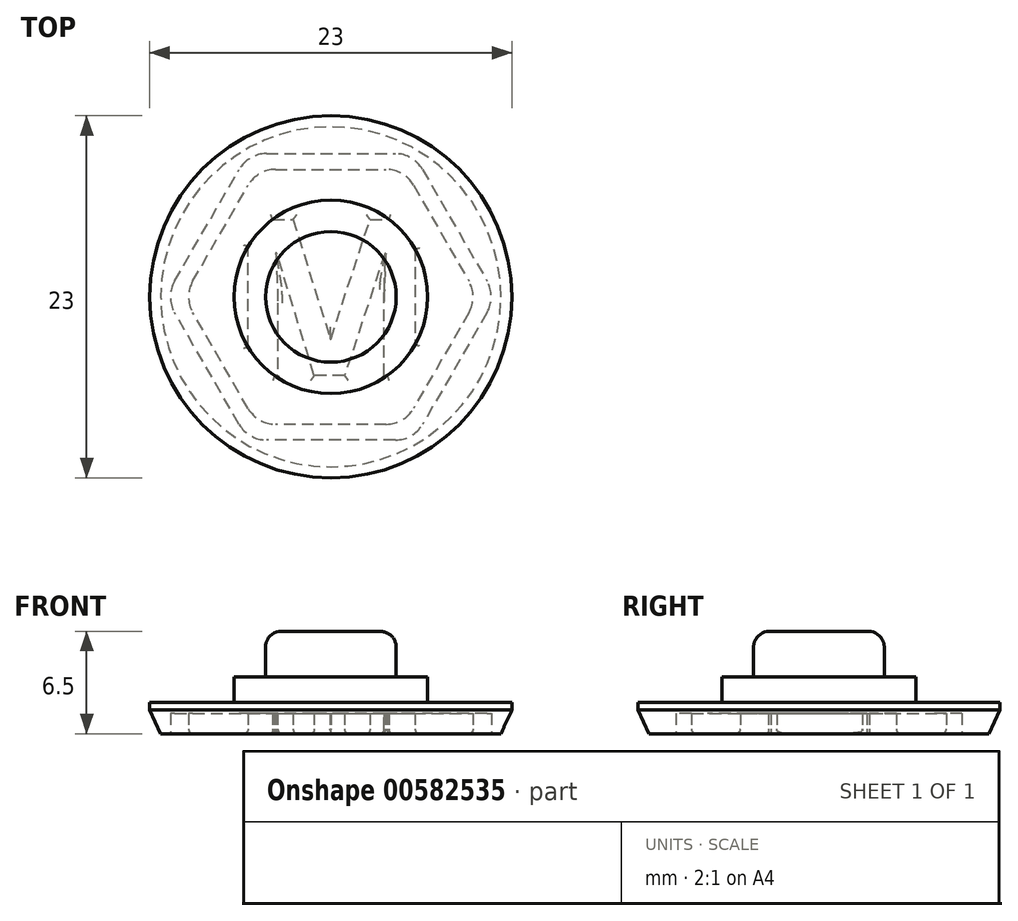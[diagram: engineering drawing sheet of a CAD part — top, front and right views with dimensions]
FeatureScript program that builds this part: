
annotation { "Feature Type Name" : "Feature", "Feature Type Description" : "" }
export const myFeature = defineFeature(function(context is Context, id is Id, definition is map)
    precondition{}
    {
        {
            var Q0;
            Q0=qCreatedBy(makeId("Top.planeOp"),FACE);
            var sketch = newSketch(context, id + "F0", { "sketchPlane" : qUnion([Q0])});
            skCircle(sketch, "E0", {"center": v(0, 0) * mm, "radius": 11.5 * mm});
            skCircle(sketch, "E1", {"center": v(0, 0) * mm, "radius": 4.15 * mm});
            skCircle(sketch, "E2.0", {"center": v(0, 0) * mm, "radius": 6.15 * mm});
            skSolve(sketch);
        }
        {
            var Q0;
            Q0=makeQuery(id+"F0.imprint","IMPRINT",FACE,{"disambiguationData":[TD([[makeQuery(id+"F0.imprint","IMPRINT",EDGE,{"derivedFrom":sQuery(id+"F0.wireOp",EDGE,"E0")}),1.0]])]});
            extrude(context, id + "F1", {"entities" : qUnion([Q0]), "depth" : 2 * mm, "offsetDistance" : 25 * mm});
        }
        {
            var Q0;
            Q0=makeQuery(id+"F0.imprint","IMPRINT",FACE,{"disambiguationData":[TD([[makeQuery(id+"F0.imprint","IMPRINT",EDGE,{"derivedFrom":sQuery(id+"F0.wireOp",EDGE,"E1")}),-1.0]])]});
            extrude(context, id + "F2", {"entities" : qUnion([Q0]), "operationType" : NewBodyOperationType.ADD, "depth" : 3.6 * mm, "offsetDistance" : 25 * mm});
        }
        {
            var Q0;
            Q0=makeQuery(id+"F0.imprint","IMPRINT",FACE,{"disambiguationData":[TD([[makeQuery(id+"F0.imprint","IMPRINT",EDGE,{"derivedFrom":sQuery(id+"F0.wireOp",EDGE,"E1")}),1.0]])]});
            extrude(context, id + "F3", {"entities" : qUnion([Q0]), "operationType" : NewBodyOperationType.ADD, "depth" : 6.5 * mm, "offsetDistance" : 25 * mm});
        }
        {
            var Q0;
            Q0=makeQuery(id+"F0.imprint","IMPRINT",FACE,{"disambiguationData":[TD([[makeQuery(id+"F0.imprint","IMPRINT",EDGE,{"derivedFrom":sQuery(id+"F0.wireOp",EDGE,"E0")}),1.0]])]});
            var sketch = newSketch(context, id + "F4", { "sketchPlane" : qUnion([Q0])});
            skCircle(sketch, "E3.cCircle", {"center": v(0, 0) * mm, "radius": 9.1 * mm, "construction": true});
            skLineSegment(sketch, "E3.0", {"start": v(9.92, -1) * mm, "end": v(5.83, -8.1) * mm});
            skLineSegment(sketch, "E3.1", {"start": v(4.1, -9.1) * mm, "end": v(-4.1, -9.1) * mm});
            skLineSegment(sketch, "E3.2", {"start": v(-5.83, -8.1) * mm, "end": v(-9.92, -1) * mm});
            skLineSegment(sketch, "E3.3", {"start": v(-9.92, 1) * mm, "end": v(-5.83, 8.1) * mm});
            skLineSegment(sketch, "E3.4", {"start": v(-4.1, 9.1) * mm, "end": v(4.1, 9.1) * mm});
            skLineSegment(sketch, "E3.5", {"start": v(5.83, 8.1) * mm, "end": v(9.92, 1) * mm});
            skPoint(sketch, "E3.0.midPoint", {"position": v(7.87, -4.55) * mm});
            skLineSegment(sketch, "E4.0", {"start": v(5.25, 7.1) * mm, "end": v(8.77, 1) * mm});
            skLineSegment(sketch, "E4.1", {"start": v(3.52, -8.1) * mm, "end": v(-3.52, -8.1) * mm});
            skLineSegment(sketch, "E4.2", {"start": v(-5.25, -7.1) * mm, "end": v(-8.77, -1) * mm});
            skLineSegment(sketch, "E4.3", {"start": v(8.77, -1) * mm, "end": v(5.25, -7.1) * mm});
            skLineSegment(sketch, "E4.4", {"start": v(-8.77, 1) * mm, "end": v(-5.25, 7.1) * mm});
            skLineSegment(sketch, "E4.5", {"start": v(-3.52, 8.1) * mm, "end": v(3.52, 8.1) * mm});
            skPoint(sketch, "E5.visualSharp", {"position": v(10.5, 0) * mm});
            skArc(sketch, "E5.filletArc", {"start": v(9.92, -1) * mm, "mid": v(10.2, 0) * mm, "end": v(9.92, 1) * mm});
            skPoint(sketch, "E6.visualSharp", {"position": v(5.25, 9.1) * mm});
            skArc(sketch, "E6.filletArc", {"start": v(5.83, 8.1) * mm, "mid": v(5.1, 8.83) * mm, "end": v(4.1, 9.1) * mm});
            skPoint(sketch, "E7.visualSharp", {"position": v(-5.25, 9.1) * mm});
            skArc(sketch, "E7.filletArc", {"start": v(-4.1, 9.1) * mm, "mid": v(-5.1, 8.83) * mm, "end": v(-5.83, 8.1) * mm});
            skPoint(sketch, "E8.visualSharp", {"position": v(-10.5, 0) * mm});
            skArc(sketch, "E8.filletArc", {"start": v(-9.92, 1) * mm, "mid": v(-10.2, 0) * mm, "end": v(-9.92, -1) * mm});
            skPoint(sketch, "E9.visualSharp", {"position": v(-5.25, -9.1) * mm});
            skArc(sketch, "E9.filletArc", {"start": v(-5.83, -8.1) * mm, "mid": v(-5.1, -8.83) * mm, "end": v(-4.1, -9.1) * mm});
            skPoint(sketch, "E10.visualSharp", {"position": v(5.25, -9.1) * mm});
            skArc(sketch, "E10.filletArc", {"start": v(4.1, -9.1) * mm, "mid": v(5.1, -8.83) * mm, "end": v(5.83, -8.1) * mm});
            skPoint(sketch, "E11.visualSharp", {"position": v(4.67, -8.1) * mm});
            skArc(sketch, "E11.filletArc", {"start": v(3.52, -8.1) * mm, "mid": v(4.52, -7.83) * mm, "end": v(5.25, -7.1) * mm});
            skPoint(sketch, "E12.visualSharp", {"position": v(4.67, 8.1) * mm});
            skArc(sketch, "E12.filletArc", {"start": v(5.25, 7.1) * mm, "mid": v(4.52, 7.83) * mm, "end": v(3.52, 8.1) * mm});
            skPoint(sketch, "E13.visualSharp", {"position": v(-4.67, 8.1) * mm});
            skArc(sketch, "E13.filletArc", {"start": v(-3.52, 8.1) * mm, "mid": v(-4.52, 7.83) * mm, "end": v(-5.25, 7.1) * mm});
            skPoint(sketch, "E14.visualSharp", {"position": v(-9.35, 0) * mm});
            skArc(sketch, "E14.filletArc", {"start": v(-8.77, 1) * mm, "mid": v(-9.04, 0) * mm, "end": v(-8.77, -1) * mm});
            skPoint(sketch, "E15.visualSharp", {"position": v(-4.67, -8.1) * mm});
            skArc(sketch, "E15.filletArc", {"start": v(-5.25, -7.1) * mm, "mid": v(-4.52, -7.83) * mm, "end": v(-3.52, -8.1) * mm});
            skPoint(sketch, "E16.visualSharp", {"position": v(9.35, 0) * mm});
            skArc(sketch, "E16.filletArc", {"start": v(8.77, -1) * mm, "mid": v(9.04, 0) * mm, "end": v(8.77, 1) * mm});
            skText(sketch, "E17", { "text": "M", "fontName": "OpenSans-Bold.ttf"});
            const initialGuessF4  = {"E17": [-0.0065, -0.005, 1, 0, 0.01]};
            skSetInitialGuess(sketch, initialGuessF4);
            skSolve(sketch);
        }
        {
            var Q0;
            Q0=makeQuery(id+"F4.imprint","IMPRINT",FACE,{"disambiguationData":[TD([[makeQuery(id+"F4.imprint","IMPRINT",EDGE,{"derivedFrom":sQuery(id+"F4.wireOp",EDGE,"E17.sketch_text.stroke-0")}),-1.0]])]});
            var Q1;
            Q1=makeQuery(id+"F4.imprint","IMPRINT",FACE,{"disambiguationData":[TD([[makeQuery(id+"F4.imprint","IMPRINT",EDGE,{"derivedFrom":sQuery(id+"F4.wireOp",EDGE,"E3.0")}),-1.0]])]});
            extrude(context, id + "F5", {"entities" : qUnion([Q0, Q1]), "operationType" : NewBodyOperationType.REMOVE, "depth" : 1.3 * mm, "offsetDistance" : 25 * mm});
        }
        {
            var Q0;
            Q0=makeQuery(id+"F1.opExtrude","CAP_EDGE",EDGE,{"disambiguationData":[OSD([sQuery(id+"F0.wireOp",EDGE,"E0")])],"isStart":true});
            chamfer(context, id + "F6", {"entities" : qUnion([Q0]), "chamferType" : ChamferType.TWO_OFFSETS, "width1" : 1.5 * mm, "oppositeDirection" : false, "width2" : 0.7 * mm, "tangentPropagation" : true});
        }
        {
            var Q0;
            Q0=makeQuery(id+"F3.opExtrude","CAP_EDGE",EDGE,{"disambiguationData":[OSD([sQuery(id+"F0.wireOp",EDGE,"E1")])],"isStart":false});
            fillet(context, id + "F7", {"entities" : qUnion([Q0]), "radius" : 1 * mm, "tangentPropagation" : true, "allowEdgeOverflow" : false});
        }
        {
            var Q0;
            Q0=makeQuery(id+"F5.boolean.opBoolean","COPY",EDGE,{"derivedFrom":makeQuery(id+"F5.opExtrude","CAP_EDGE",EDGE,{"disambiguationData":[OSD([sQuery(id+"F4.wireOp",EDGE,"E3.5")])],"isStart":true})});
            var Q1;
            Q1=makeQuery(id+"F5.boolean.opBoolean","COPY",EDGE,{"derivedFrom":makeQuery(id+"F5.opExtrude","CAP_EDGE",EDGE,{"disambiguationData":[OSD([sQuery(id+"F4.wireOp",EDGE,"E4.3")])],"isStart":true})});
            var Q2;
            Q2=makeQuery(id+"F5.boolean.opBoolean","COPY",EDGE,{"derivedFrom":makeQuery(id+"F5.opExtrude","CAP_EDGE",EDGE,{"disambiguationData":[OSD([sQuery(id+"F4.wireOp",EDGE,"4fd293f3-2c2e-4eb3-8031-e35e885f4dbc.sketch_text.stroke-5")])],"isStart":true})});
            var Q3;
            Q3=makeQuery(id+"F5.boolean.opBoolean","COPY",EDGE,{"derivedFrom":makeQuery(id+"F5.opExtrude","CAP_EDGE",EDGE,{"disambiguationData":[OSD([sQuery(id+"F4.wireOp",EDGE,"4fd293f3-2c2e-4eb3-8031-e35e885f4dbc.sketch_text.stroke-11")])],"isStart":true})});
            var Q4;
            Q4=makeQuery(id+"F5.boolean.opBoolean","COPY",EDGE,{"derivedFrom":makeQuery(id+"F5.opExtrude","CAP_EDGE",EDGE,{"disambiguationData":[OSD([sQuery(id+"F4.wireOp",EDGE,"4fd293f3-2c2e-4eb3-8031-e35e885f4dbc.sketch_text.stroke-10")])],"isStart":true})});
            var Q5;
            Q5=makeQuery(id+"F5.boolean.opBoolean","COPY",EDGE,{"derivedFrom":makeQuery(id+"F5.opExtrude","CAP_EDGE",EDGE,{"disambiguationData":[OSD([sQuery(id+"F4.wireOp",EDGE,"4fd293f3-2c2e-4eb3-8031-e35e885f4dbc.sketch_text.stroke-9")])],"isStart":true})});
            var Q6;
            Q6=makeQuery(id+"F5.boolean.opBoolean","COPY",EDGE,{"derivedFrom":makeQuery(id+"F5.opExtrude","CAP_EDGE",EDGE,{"disambiguationData":[OSD([sQuery(id+"F4.wireOp",EDGE,"4fd293f3-2c2e-4eb3-8031-e35e885f4dbc.sketch_text.stroke-7")])],"isStart":true})});
            var Q7;
            Q7=makeQuery(id+"F5.boolean.opBoolean","COPY",EDGE,{"derivedFrom":makeQuery(id+"F5.opExtrude","CAP_EDGE",EDGE,{"disambiguationData":[OSD([sQuery(id+"F4.wireOp",EDGE,"4fd293f3-2c2e-4eb3-8031-e35e885f4dbc.sketch_text.stroke-6")])],"isStart":true})});
            var Q8;
            Q8=makeQuery(id+"F5.boolean.opBoolean","COPY",EDGE,{"derivedFrom":makeQuery(id+"F5.opExtrude","CAP_EDGE",EDGE,{"disambiguationData":[OSD([sQuery(id+"F4.wireOp",EDGE,"4fd293f3-2c2e-4eb3-8031-e35e885f4dbc.sketch_text.stroke-3")])],"isStart":true})});
            var Q9;
            Q9=makeQuery(id+"F5.boolean.opBoolean","COPY",EDGE,{"derivedFrom":makeQuery(id+"F5.opExtrude","CAP_EDGE",EDGE,{"disambiguationData":[OSD([sQuery(id+"F4.wireOp",EDGE,"4fd293f3-2c2e-4eb3-8031-e35e885f4dbc.sketch_text.stroke-0")])],"isStart":true})});
            var Q10;
            Q10=makeQuery(id+"F5.boolean.opBoolean","COPY",EDGE,{"derivedFrom":makeQuery(id+"F5.opExtrude","CAP_EDGE",EDGE,{"disambiguationData":[OSD([sQuery(id+"F4.wireOp",EDGE,"4fd293f3-2c2e-4eb3-8031-e35e885f4dbc.sketch_text.stroke-17")])],"isStart":true})});
            var Q11;
            Q11=makeQuery(id+"F5.boolean.opBoolean","COPY",EDGE,{"derivedFrom":makeQuery(id+"F5.opExtrude","CAP_EDGE",EDGE,{"disambiguationData":[OSD([sQuery(id+"F4.wireOp",EDGE,"4fd293f3-2c2e-4eb3-8031-e35e885f4dbc.sketch_text.stroke-16")])],"isStart":true})});
            var Q12;
            Q12=makeQuery(id+"F5.boolean.opBoolean","COPY",EDGE,{"derivedFrom":makeQuery(id+"F5.opExtrude","CAP_EDGE",EDGE,{"disambiguationData":[OSD([sQuery(id+"F4.wireOp",EDGE,"4fd293f3-2c2e-4eb3-8031-e35e885f4dbc.sketch_text.stroke-13")])],"isStart":true})});
            var Q13;
            Q13=makeQuery(id+"F5.boolean.opBoolean","COPY",EDGE,{"derivedFrom":makeQuery(id+"F5.opExtrude","CAP_EDGE",EDGE,{"disambiguationData":[OSD([sQuery(id+"F4.wireOp",EDGE,"4fd293f3-2c2e-4eb3-8031-e35e885f4dbc.sketch_text.stroke-12")])],"isStart":true})});
            fillet(context, id + "F8", {"entities" : qUnion([Q0, Q1, Q2, Q3, Q4, Q5, Q6, Q7, Q8, Q9, Q10, Q11, Q12, Q13]), "radius" : 0.3 * mm, "tangentPropagation" : true, "allowEdgeOverflow" : false});
        }
        {
            var Q0;
            {var subQ0=sQuery(id+"F0.wireOp",EDGE,"E2.0");var subQ1=makeQuery(id+"F0.imprint","IMPRINT",EDGE,{"derivedFrom":subQ0});Q0=makeQuery(id+"F5.boolean.opBoolean","COPY",EDGE,{"derivedFrom":makeQuery(id+"F5.opExtrude","CAP_EDGE",EDGE,{"disambiguationData":[OSD([subQ0]),TDD([makeQuery(id+"F4.imprint","IMPRINT",EDGE,{"disambiguationData":[TD([[makeQuery(id+"F4.imprint","INTERSECT",VERTEX,{"derivedFrom":[subQ1,sQuery(id+"F4.wireOp",EDGE,"E17.sketch_text.stroke-4")]}),1.0]])],"derivedFrom":subQ1})])],"isStart":true})});}
            var Q1;
            Q1=makeQuery(id+"F5.boolean.opBoolean","COPY",EDGE,{"derivedFrom":makeQuery(id+"F5.opExtrude","CAP_EDGE",EDGE,{"disambiguationData":[OSD([sQuery(id+"F4.wireOp",EDGE,"E17.sketch_text.stroke-5")])],"isStart":true})});
            var Q2;
            Q2=makeQuery(id+"F5.boolean.opBoolean","COPY",EDGE,{"derivedFrom":makeQuery(id+"F5.opExtrude","CAP_EDGE",EDGE,{"disambiguationData":[OSD([sQuery(id+"F4.wireOp",EDGE,"E17.sketch_text.stroke-3")])],"isStart":true})});
            var Q3;
            Q3=makeQuery(id+"F5.boolean.opBoolean","COPY",EDGE,{"derivedFrom":makeQuery(id+"F5.opExtrude","CAP_EDGE",EDGE,{"disambiguationData":[OSD([sQuery(id+"F4.wireOp",EDGE,"E17.sketch_text.stroke-0")])],"isStart":true})});
            var Q4;
            Q4=makeQuery(id+"F5.boolean.opBoolean","COPY",EDGE,{"derivedFrom":makeQuery(id+"F5.opExtrude","CAP_EDGE",EDGE,{"disambiguationData":[OSD([sQuery(id+"F4.wireOp",EDGE,"E17.sketch_text.stroke-18")])],"isStart":true})});
            var Q5;
            Q5=makeQuery(id+"F5.boolean.opBoolean","COPY",EDGE,{"derivedFrom":makeQuery(id+"F5.opExtrude","CAP_EDGE",EDGE,{"disambiguationData":[OSD([sQuery(id+"F4.wireOp",EDGE,"E17.sketch_text.stroke-17")])],"isStart":true})});
            var Q6;
            Q6=makeQuery(id+"F5.boolean.opBoolean","COPY",EDGE,{"derivedFrom":makeQuery(id+"F5.opExtrude","CAP_EDGE",EDGE,{"disambiguationData":[OSD([sQuery(id+"F4.wireOp",EDGE,"E17.sketch_text.stroke-13")])],"isStart":true})});
            var Q7;
            {var subQ0=sQuery(id+"F0.wireOp",EDGE,"E2.0");var subQ1=makeQuery(id+"F0.imprint","IMPRINT",EDGE,{"derivedFrom":subQ0});Q7=makeQuery(id+"F5.boolean.opBoolean","COPY",EDGE,{"derivedFrom":makeQuery(id+"F5.opExtrude","CAP_EDGE",EDGE,{"disambiguationData":[OSD([subQ0]),TDD([makeQuery(id+"F4.imprint","IMPRINT",EDGE,{"disambiguationData":[TD([[makeQuery(id+"F4.imprint","INTERSECT",VERTEX,{"disambiguationData":[OD(1.0)],"derivedFrom":[subQ1,sQuery(id+"F4.wireOp",EDGE,"E17.sketch_text.stroke-11")]}),1.0]])],"derivedFrom":subQ1})])],"isStart":true})});}
            var Q8;
            Q8=makeQuery(id+"F5.boolean.opBoolean","COPY",EDGE,{"derivedFrom":makeQuery(id+"F5.opExtrude","CAP_EDGE",EDGE,{"disambiguationData":[OSD([sQuery(id+"F4.wireOp",EDGE,"E17.sketch_text.stroke-11")])],"isStart":true})});
            var Q9;
            {var subQ0=sQuery(id+"F0.wireOp",EDGE,"E2.0");var subQ1=makeQuery(id+"F0.imprint","IMPRINT",EDGE,{"derivedFrom":subQ0});Q9=makeQuery(id+"F5.boolean.opBoolean","COPY",EDGE,{"derivedFrom":makeQuery(id+"F5.opExtrude","CAP_EDGE",EDGE,{"disambiguationData":[OSD([subQ0]),TDD([makeQuery(id+"F4.imprint","IMPRINT",EDGE,{"disambiguationData":[TD([[makeQuery(id+"F4.imprint","INTERSECT",VERTEX,{"derivedFrom":[subQ1,sQuery(id+"F4.wireOp",EDGE,"E17.sketch_text.stroke-10")]}),1.0]])],"derivedFrom":subQ1})])],"isStart":true})});}
            var Q10;
            Q10=makeQuery(id+"F5.boolean.opBoolean","COPY",EDGE,{"derivedFrom":makeQuery(id+"F5.opExtrude","CAP_EDGE",EDGE,{"disambiguationData":[OSD([sQuery(id+"F4.wireOp",EDGE,"E17.sketch_text.stroke-10")])],"isStart":true})});
            var Q11;
            Q11=makeQuery(id+"F5.boolean.opBoolean","COPY",EDGE,{"derivedFrom":makeQuery(id+"F5.opExtrude","CAP_EDGE",EDGE,{"disambiguationData":[OSD([sQuery(id+"F4.wireOp",EDGE,"E17.sketch_text.stroke-9")])],"isStart":true})});
            var Q12;
            Q12=makeQuery(id+"F5.boolean.opBoolean","COPY",EDGE,{"derivedFrom":makeQuery(id+"F5.opExtrude","CAP_EDGE",EDGE,{"disambiguationData":[OSD([sQuery(id+"F4.wireOp",EDGE,"E17.sketch_text.stroke-7")])],"isStart":true})});
            var Q13;
            Q13=makeQuery(id+"F5.boolean.opBoolean","COPY",EDGE,{"derivedFrom":makeQuery(id+"F5.opExtrude","CAP_EDGE",EDGE,{"disambiguationData":[OSD([sQuery(id+"F4.wireOp",EDGE,"E17.sketch_text.stroke-6")])],"isStart":true})});
            var Q14;
            {var subQ0=sQuery(id+"F0.wireOp",EDGE,"E2.0");var subQ1=makeQuery(id+"F0.imprint","IMPRINT",EDGE,{"derivedFrom":subQ0});Q14=makeQuery(id+"F5.boolean.opBoolean","COPY",EDGE,{"derivedFrom":makeQuery(id+"F5.opExtrude","CAP_EDGE",EDGE,{"disambiguationData":[OSD([subQ0]),TDD([makeQuery(id+"F4.imprint","IMPRINT",EDGE,{"disambiguationData":[TD([[makeQuery(id+"F4.imprint","INTERSECT",VERTEX,{"disambiguationData":[OD(1.0)],"derivedFrom":[subQ1,sQuery(id+"F4.wireOp",EDGE,"E17.sketch_text.stroke-5")]}),1.0]])],"derivedFrom":subQ1})])],"isStart":true})});}
            var Q15;
            Q15=makeQuery(id+"F5.boolean.opBoolean","COPY",EDGE,{"derivedFrom":makeQuery(id+"F5.opExtrude","CAP_EDGE",EDGE,{"disambiguationData":[OSD([sQuery(id+"F4.wireOp",EDGE,"E17.sketch_text.stroke-12")])],"isStart":true})});
            var Q16;
            Q16=makeQuery(id+"F5.boolean.opBoolean","COPY",EDGE,{"derivedFrom":makeQuery(id+"F5.opExtrude","CAP_EDGE",EDGE,{"disambiguationData":[OSD([sQuery(id+"F4.wireOp",EDGE,"E17.sketch_text.stroke-4")])],"isStart":true})});
            fillet(context, id + "F9", {"entities" : qUnion([Q0, Q1, Q2, Q3, Q4, Q5, Q6, Q7, Q8, Q9, Q10, Q11, Q12, Q13, Q14, Q15, Q16]), "radius" : 0.3 * mm, "tangentPropagation" : true, "allowEdgeOverflow" : false});
        }
    });
